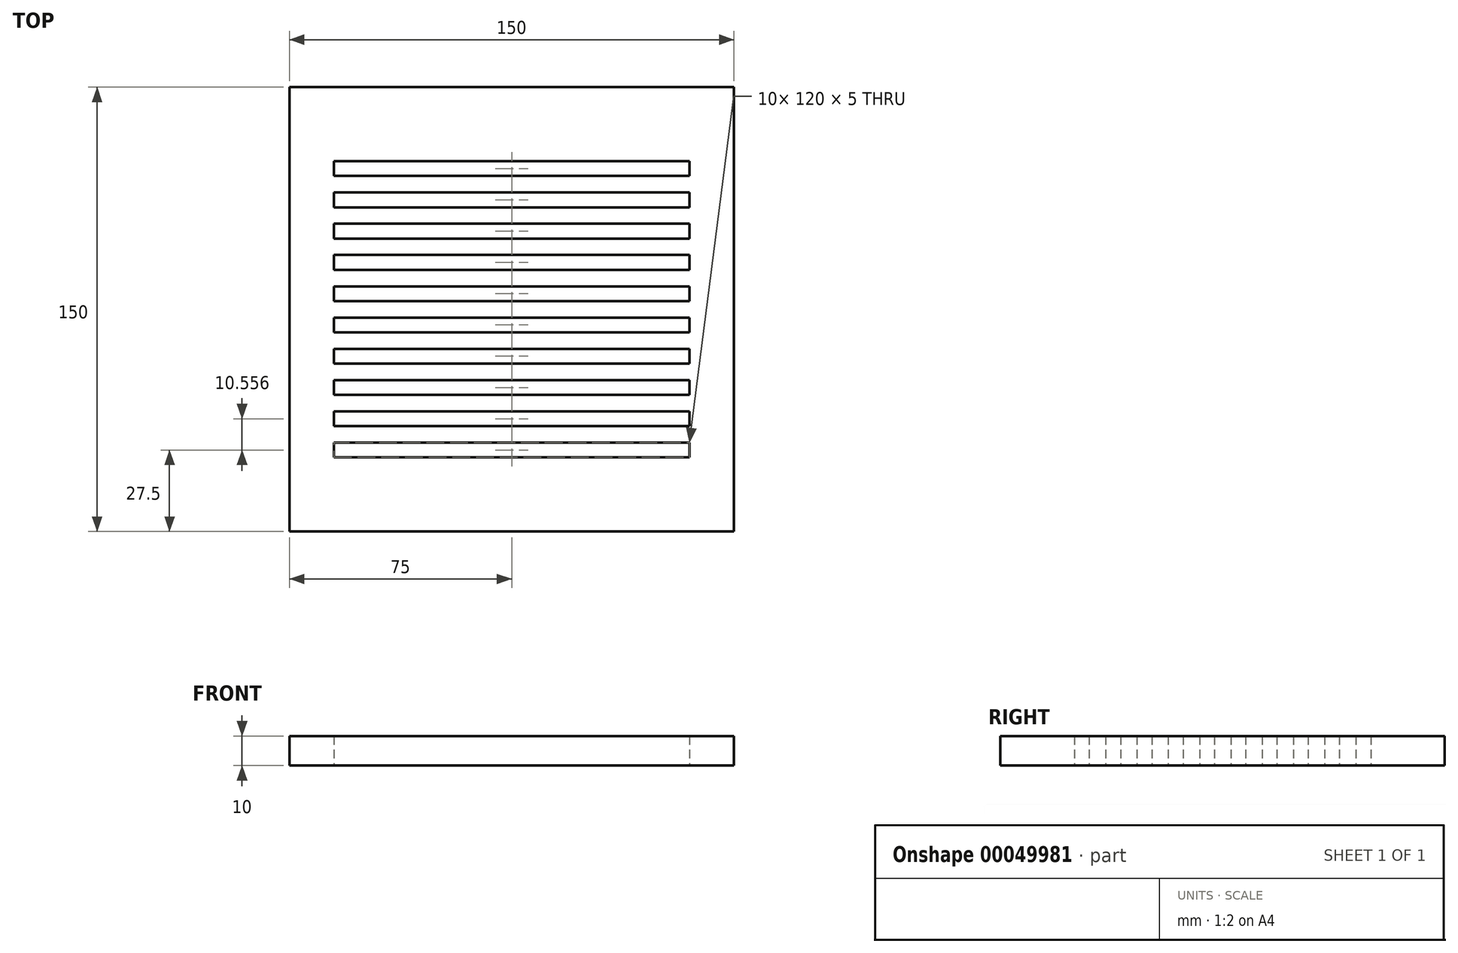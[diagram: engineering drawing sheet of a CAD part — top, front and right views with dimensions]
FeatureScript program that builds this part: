
annotation { "Feature Type Name" : "Feature", "Feature Type Description" : "" }
export const myFeature = defineFeature(function(context is Context, id is Id, definition is map)
    precondition{}
    {
        {
            var Q0;
            Q0=qCreatedBy(makeId("Top.planeOp"),FACE);
            var sketch = newSketch(context, id + "F0", { "sketchPlane" : qUnion([Q0])});
            skLineSegment(sketch, "E0.rect.bottom", {"start": v(75, 75) * mm, "end": v(-75, 75) * mm});
            skLineSegment(sketch, "E0.rect.top", {"start": v(75, -75) * mm, "end": v(-75, -75) * mm});
            skLineSegment(sketch, "E0.rect.left", {"start": v(75, 75) * mm, "end": v(75, -75) * mm});
            skLineSegment(sketch, "E0.rect.right", {"start": v(-75, 75) * mm, "end": v(-75, -75) * mm});
            skPoint(sketch, "E0.rect.middle", {"position": v(0, 0) * mm});
            skLineSegment(sketch, "E1", {"start": v(-60, 50) * mm, "end": v(60, 50) * mm});
            skLineSegment(sketch, "E2", {"start": v(60, 50) * mm, "end": v(60, 45) * mm});
            skLineSegment(sketch, "E3", {"start": v(60, 45) * mm, "end": v(-60, 45) * mm});
            skLineSegment(sketch, "E4", {"start": v(-60, 45) * mm, "end": v(-60, 50) * mm});
            skLineSegment(sketch, "E5.0.1.0", {"start": v(60, 34.44) * mm, "end": v(-60, 34.44) * mm});
            skLineSegment(sketch, "E5.0.1.1", {"start": v(-60, 39.44) * mm, "end": v(60, 39.44) * mm});
            skLineSegment(sketch, "E5.0.1.2", {"start": v(-60, 34.44) * mm, "end": v(-60, 39.44) * mm});
            skLineSegment(sketch, "E5.0.1.3", {"start": v(60, 39.44) * mm, "end": v(60, 34.44) * mm});
            skLineSegment(sketch, "E5.0.2.0", {"start": v(60, 23.89) * mm, "end": v(-60, 23.89) * mm});
            skLineSegment(sketch, "E5.0.2.1", {"start": v(-60, 28.89) * mm, "end": v(60, 28.89) * mm});
            skLineSegment(sketch, "E5.0.2.2", {"start": v(-60, 23.89) * mm, "end": v(-60, 28.89) * mm});
            skLineSegment(sketch, "E5.0.2.3", {"start": v(60, 28.89) * mm, "end": v(60, 23.89) * mm});
            skLineSegment(sketch, "E5.0.3.0", {"start": v(60, 13.33) * mm, "end": v(-60, 13.33) * mm});
            skLineSegment(sketch, "E5.0.3.1", {"start": v(-60, 18.33) * mm, "end": v(60, 18.33) * mm});
            skLineSegment(sketch, "E5.0.3.2", {"start": v(-60, 13.33) * mm, "end": v(-60, 18.33) * mm});
            skLineSegment(sketch, "E5.0.3.3", {"start": v(60, 18.33) * mm, "end": v(60, 13.33) * mm});
            skLineSegment(sketch, "E5.direction1", {"start": v(-60, 45) * mm, "end": v(-35, 45) * mm, "construction": true});
            skLineSegment(sketch, "E5.direction2", {"start": v(-60, 45) * mm, "end": v(-60, 34.44) * mm, "construction": true});
            skLineSegment(sketch, "E6.0.0.4", {"start": v(60, 2.78) * mm, "end": v(-60, 2.78) * mm});
            skLineSegment(sketch, "E6.3.0.4", {"start": v(-60, 7.78) * mm, "end": v(60, 7.78) * mm});
            skLineSegment(sketch, "E6.6.0.4", {"start": v(-60, 2.78) * mm, "end": v(-60, 7.78) * mm});
            skLineSegment(sketch, "E6.9.0.4", {"start": v(60, 7.78) * mm, "end": v(60, 2.78) * mm});
            skLineSegment(sketch, "E6.0.0.5", {"start": v(60, -7.78) * mm, "end": v(-60, -7.78) * mm});
            skLineSegment(sketch, "E6.3.0.5", {"start": v(-60, -2.78) * mm, "end": v(60, -2.78) * mm});
            skLineSegment(sketch, "E6.6.0.5", {"start": v(-60, -7.78) * mm, "end": v(-60, -2.78) * mm});
            skLineSegment(sketch, "E6.9.0.5", {"start": v(60, -2.78) * mm, "end": v(60, -7.78) * mm});
            skLineSegment(sketch, "E6.0.0.6", {"start": v(60, -18.33) * mm, "end": v(-60, -18.33) * mm});
            skLineSegment(sketch, "E6.3.0.6", {"start": v(-60, -13.33) * mm, "end": v(60, -13.33) * mm});
            skLineSegment(sketch, "E6.6.0.6", {"start": v(-60, -18.33) * mm, "end": v(-60, -13.33) * mm});
            skLineSegment(sketch, "E6.9.0.6", {"start": v(60, -13.33) * mm, "end": v(60, -18.33) * mm});
            skLineSegment(sketch, "E7.0.0.7", {"start": v(60, -28.89) * mm, "end": v(-60, -28.89) * mm});
            skLineSegment(sketch, "E7.3.0.7", {"start": v(-60, -23.89) * mm, "end": v(60, -23.89) * mm});
            skLineSegment(sketch, "E7.6.0.7", {"start": v(-60, -28.89) * mm, "end": v(-60, -23.89) * mm});
            skLineSegment(sketch, "E7.9.0.7", {"start": v(60, -23.89) * mm, "end": v(60, -28.89) * mm});
            skLineSegment(sketch, "E7.0.0.8", {"start": v(60, -39.44) * mm, "end": v(-60, -39.44) * mm});
            skLineSegment(sketch, "E7.3.0.8", {"start": v(-60, -34.44) * mm, "end": v(60, -34.44) * mm});
            skLineSegment(sketch, "E7.6.0.8", {"start": v(-60, -39.44) * mm, "end": v(-60, -34.44) * mm});
            skLineSegment(sketch, "E7.9.0.8", {"start": v(60, -34.44) * mm, "end": v(60, -39.44) * mm});
            skLineSegment(sketch, "E7.0.0.9", {"start": v(60, -50) * mm, "end": v(-60, -50) * mm});
            skLineSegment(sketch, "E7.3.0.9", {"start": v(-60, -45) * mm, "end": v(60, -45) * mm});
            skLineSegment(sketch, "E7.6.0.9", {"start": v(-60, -50) * mm, "end": v(-60, -45) * mm});
            skLineSegment(sketch, "E7.9.0.9", {"start": v(60, -45) * mm, "end": v(60, -50) * mm});
            skSolve(sketch);
        }
        {
            var Q0;
            Q0=makeQuery(id+"F0.imprint","IMPRINT",FACE,{"disambiguationData":[TD([[makeQuery(id+"F0.imprint","IMPRINT",EDGE,{"derivedFrom":sQuery(id+"F0.wireOp",EDGE,"E0.rect.bottom")}),1.0]])]});
            extrude(context, id + "F1", {"entities" : qUnion([Q0]), "depth" : 10 * mm});
        }
    });
